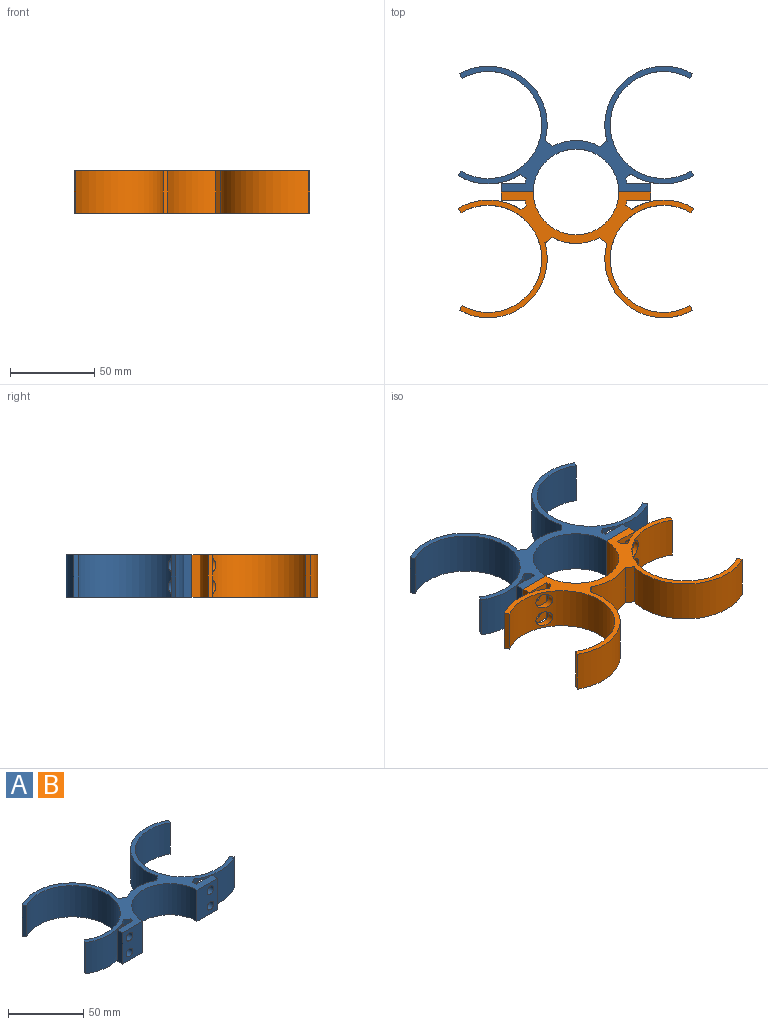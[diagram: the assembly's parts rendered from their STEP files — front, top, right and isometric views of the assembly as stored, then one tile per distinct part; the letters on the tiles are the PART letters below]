
ASSEMBLY  parts=2 mates=1
PART A: 34 faces, bbox 139.8x74.6x25.4 mm
  f0: cylinder r=31.75mm len=63.5mm, axis (0,0,-1), area 3220mm2, adj f4,f19,f20,f21,f32,f33
  f1: cylinder r=34.92mm len=37.06mm, axis (0,0,-1), area 836.4mm2, adj f4,f5,f20,f21,f32,f33
  f2: cylinder r=34.92mm len=37.27mm, axis (0,0,-1), area 842.9mm2, adj f11,f12,f20,f21,f30,f31
  f3: cylinder r=31.75mm len=63.5mm, axis (0,0,-1), area 3218.1mm2, adj f12,f13,f20,f21,f30,f31
  f4: plane 25.4x2.73mm, normal (-0.86,0.51,0), area 80.6mm2, adj f0,f1,f20,f21
  f5: plane 25.4x3.37mm, normal (-0.62,-0.78,0), area 109.7mm2, adj f1,f6,f20,f21
  f6: cylinder r=30.48mm len=25.4mm, axis (0,0,-1), area 70.1mm2, adj f5,f20,f21,f26
  f7: plane 25.4x19.05mm, normal (0,-1,0), area 420.5mm2, adj f8,f20,f21,f27,f28,f29
  f8: cylinder r=25.4mm len=50.8mm, axis (0,0,-1), area 2026.8mm2, adj f7,f9,f20,f21
  f9: plane 25.4x19.05mm, normal (0,-1,0), area 420.5mm2, adj f8,f20,f21,f23,f24,f25
  f10: cylinder r=30.48mm len=25.4mm, axis (0,0,-1), area 76.8mm2, adj f11,f20,f21,f22
  f11: plane 25.4x3.23mm, normal (0.62,-0.78,0), area 105mm2, adj f2,f10,f20,f21
  f12: plane 25.4x2.73mm, normal (0.86,0.51,0), area 80.6mm2, adj f2,f3,f20,f21
  f13: plane 25.4x2.77mm, normal (0.87,-0.49,0), area 80.6mm2, adj f3,f14,f20,f21
  f14: cylinder r=34.92mm len=51.94mm, axis (0,0,-1), area 2089.2mm2, adj f13,f15,f20,f21
  f15: plane 25.4x4.08mm, normal (-0.62,0.78,0), area 132.7mm2, adj f14,f16,f20,f21
  f16: cylinder r=30.48mm len=28.38mm, axis (0,0,-1), area 749.8mm2, adj f15,f17,f20,f21
  f17: plane 25.4x4.24mm, normal (0.62,0.78,0), area 138mm2, adj f16,f18,f20,f21
  f18: cylinder r=34.92mm len=51.94mm, axis (0,0,-1), area 2082.6mm2, adj f17,f19,f20,f21
  f19: plane 25.4x2.77mm, normal (-0.87,-0.49,0), area 80.6mm2, adj f0,f18,f20,f21
  f20: plane 139.81x74.61mm, normal (0,0,1), area 1553.1mm2, adj f0,f1,f2,f3,f4,f5,f6,f7
  f21: plane 139.81x74.61mm, normal (0,0,-1), area 1553.1mm2, adj f0,f1,f2,f3,f4,f5,f6,f7
  f22: plane 25.4x14.4mm, normal (0,1,0), area 302.3mm2, adj f10,f20,f21,f23,f24,f25
  f23: plane 25.4x5.08mm, normal (1,0,0), area 129mm2, adj f9,f20,f21,f22
  f24: cylinder r=3.17mm len=6.35mm, axis (0,-1,0), area 101.3mm2, adj f9,f22
  f25: cylinder r=3.17mm len=6.35mm, axis (0,-1,0), area 101.3mm2, adj f9,f22
  f26: plane 25.4x14.4mm, normal (0,1,0), area 302.3mm2, adj f6,f20,f21,f27,f28,f29
  f27: plane 25.4x5.08mm, normal (-1,0,0), area 129mm2, adj f7,f20,f21,f26
  f28: cylinder r=3.17mm len=6.35mm, axis (0,-1,0), area 101.3mm2, adj f7,f26
  f29: cylinder r=3.17mm len=6.35mm, axis (0,-1,0), area 101.3mm2, adj f7,f26
  f30: cylinder r=4.76mm len=9.53mm, axis (0,-1,0), area 105.7mm2, adj f2,f3
  f31: cylinder r=4.76mm len=9.53mm, axis (0,-1,0), area 105.7mm2, adj f2,f3
  f32: cylinder r=4.76mm len=9.53mm, axis (0,-1,0), area 105.6mm2, adj f0,f1
  f33: cylinder r=4.76mm len=9.53mm, axis (0,-1,0), area 105.6mm2, adj f0,f1
PART B: same geometry as A
PLACE A t=(-53.89,4.01,-100.32)mm
PLACE B rot(axis=(0,0,-1),180deg) t=(-53.89,4.01,-100.32)mm
MATE fastened B.f33 <-> A.f25  axis (0,1,0) through (-15.79,4.01,-81.27)mm
